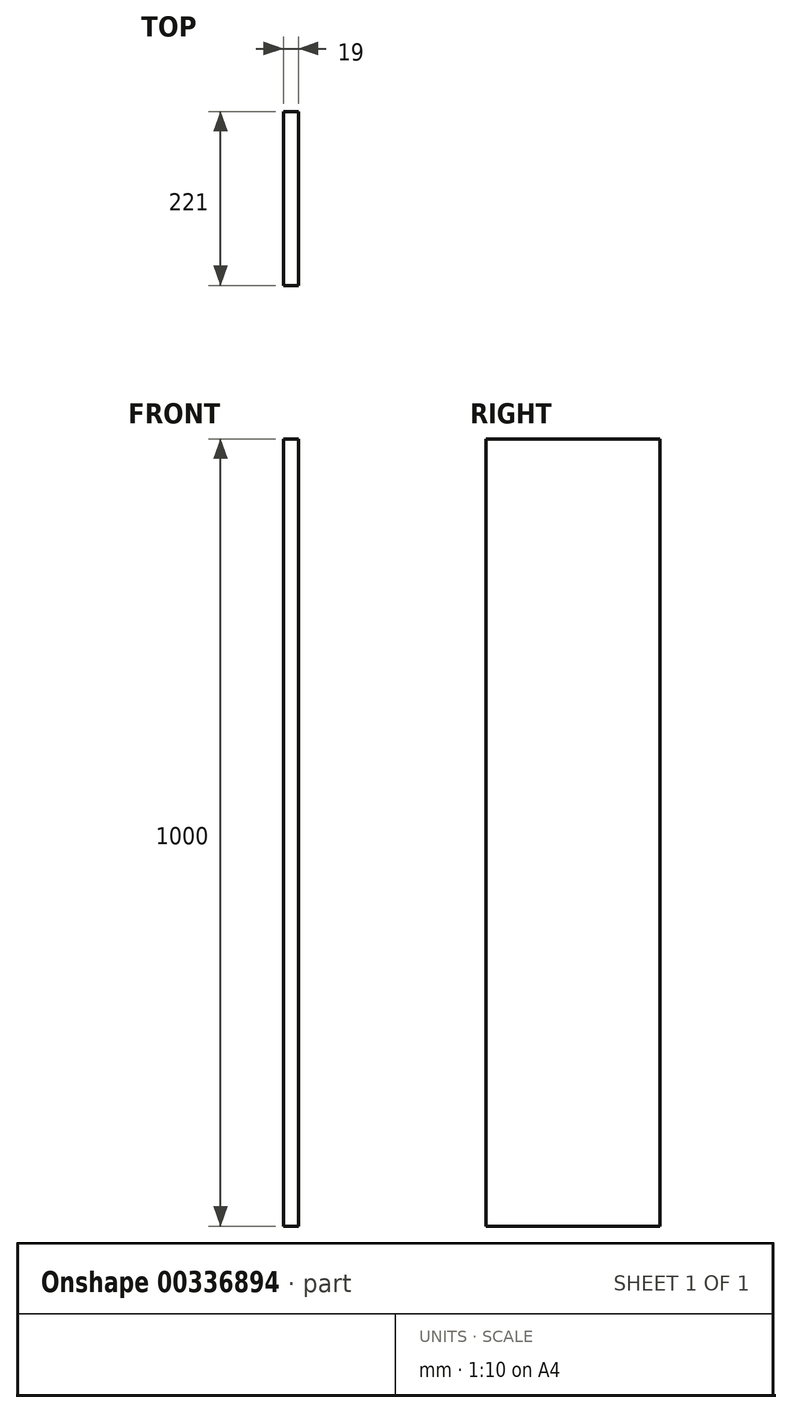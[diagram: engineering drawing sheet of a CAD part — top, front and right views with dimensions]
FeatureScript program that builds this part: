
annotation { "Feature Type Name" : "Feature", "Feature Type Description" : "" }
export const myFeature = defineFeature(function(context is Context, id is Id, definition is map)
    precondition{}
    {
        {
            var Q0;
            Q0=qCreatedBy(makeId("Right.planeOp"),FACE);
            var sketch = newSketch(context, id + "F0", { "sketchPlane" : qUnion([Q0])});
            skLineSegment(sketch, "E0.bottom", {"start": v(-110.5, 500) * mm, "end": v(110.5, 500) * mm});
            skLineSegment(sketch, "E0.top", {"start": v(-110.5, -500) * mm, "end": v(110.5, -500) * mm});
            skLineSegment(sketch, "E0.left", {"start": v(-110.5, 500) * mm, "end": v(-110.5, -500) * mm});
            skLineSegment(sketch, "E0.right", {"start": v(110.5, 500) * mm, "end": v(110.5, -500) * mm});
            skPoint(sketch, "E0.middle", {"position": v(0, 0) * mm});
            skSolve(sketch);
        }
        {
            var Q0;
            Q0 = qSketchRegion(id + "F0", true);
            extrude(context, id + "F1", {"entities" : qUnion([Q0]), "depth" : 19 * mm});
        }
    });
